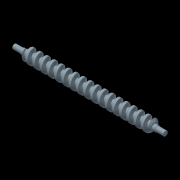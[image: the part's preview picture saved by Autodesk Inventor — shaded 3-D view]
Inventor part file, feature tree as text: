
AUTODESK INVENTOR PART (.ipt)
format: ipt  version: 2020 (Build 240168000, 168)  size: 935,936 bytes
history: native  units: mm
features: revolve x2, mirror x2, other x1, chamfer x1, helix x1, fillet x1, sketch x1
ambient origin geometry x8: Origin, YZ Plane, XZ Plane, XY Plane, X Axis, Y Axis, Z Axis, Center Point
bodies: Body1 (feature_tree)
feature tree (9):
  other  "實體1"
  revolve  "Revolution1"  [1 undecoded]
  mirror  "Mirror1"
  chamfer  "Chamfer2"  Distance=1.75mm
  helix  "Coil3"  [1 undecoded]
  revolve  "Revolution2"  [1 undecoded]
  mirror  "Mirror2"
  fillet  "Fillet5"  [1 undecoded]
  sketch  "Sketch6"  dims[d0=2.0mm d1=40.0mm d4=1.75mm d5=1.5mm d7=5.0mm d8=90.0deg d38=0.1mm d39=2.0mm d40=45.0deg d43=2.0mm d54=2.0mm d57=3.490659mm d58=1.5mm d59=3.0mm d60=4.5mm d61=10.0mm d62=190.0mm d63=0.0mm d64=90.0deg d65=90.0deg d66=0.0mm d67=0.0mm d72=45.0deg d73=2.5mm d74=90.0deg d75=3.0mm d76=0.3mm d77=2.27206mm d78=4.0mm d79=2.0mm]
note: 4 required parameter values undecoded (feature->parameter linkage not recoverable at this tier; creation-order binding heuristic only, values carry confidence <= 0.55)